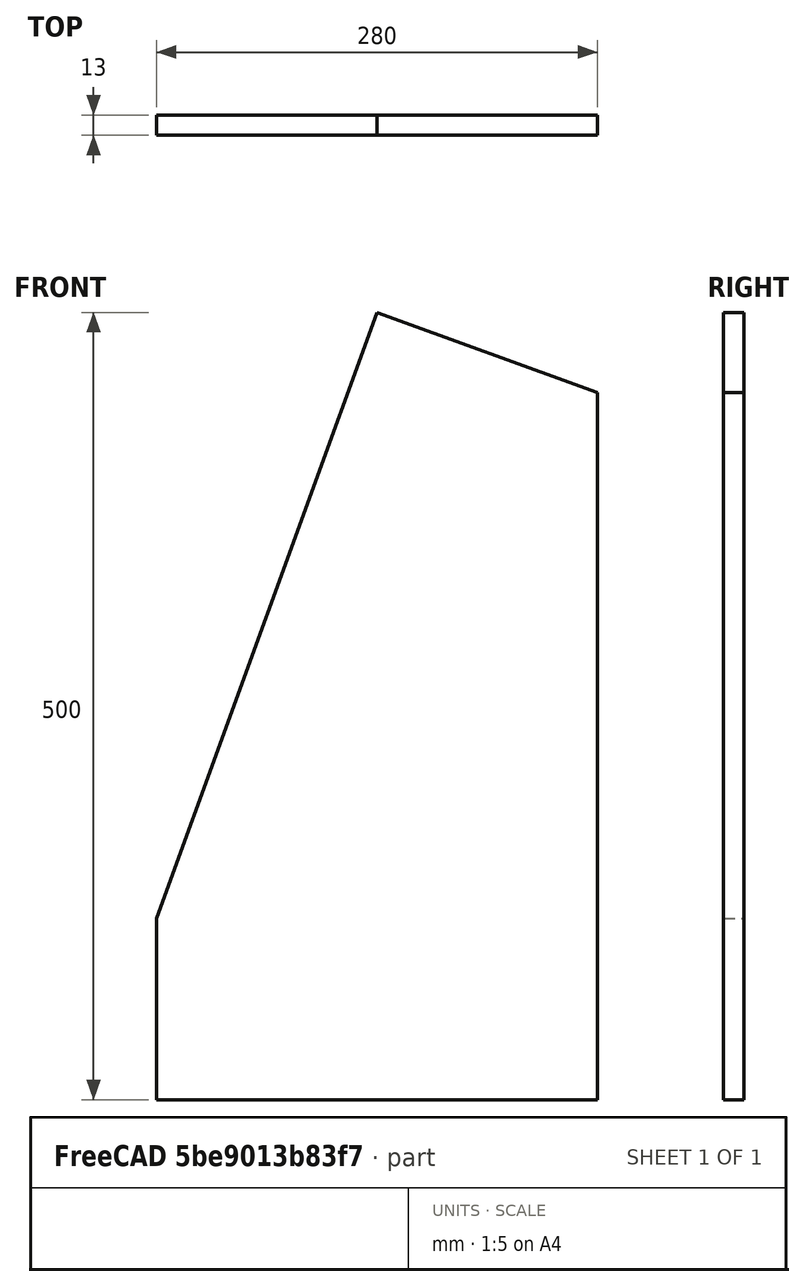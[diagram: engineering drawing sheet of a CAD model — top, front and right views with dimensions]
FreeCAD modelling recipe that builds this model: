
FCSTD DOCUMENT  (FreeCAD 0.18R14555 (Git shallow))
Label: 4000_Body_Side
License: All rights reserved
LicenseURL: http://en.wikipedia.org/wiki/All_rights_reserved
objects: Sketcher::SketchObject×1, PartDesign::Pad×1, PartDesign::Body×1, Spreadsheet::Sheet×1
note: 4 computed .brp shape members not serialized (recipe doc carries the construction recipe); baked Part::Feature solids carry a one-line shape summary decoded from their .brp

FEATURE [Sketcher::SketchObject] Sketch  label="SideWall"
  MapMode = 5
  Placement = pos=(0,0,0) rot=(1,0,0;1.5708rad)
  Support = -> [XZ_Plane]
  expr: Constraints[1] = XLS.FH
  expr: Constraints[9] = XLS.TH
  expr: Constraints[3] = XLS.TW
  sketch-geometry (7):
    g0: LineSegment StartX=0 StartY=0 StartZ=0 EndX=280 EndY=0 EndZ=0
    g1: LineSegment StartX=280 StartY=449.091 StartZ=0 EndX=140.129 EndY=500 EndZ=0
    g2: LineSegment StartX=140.129 StartY=500 StartZ=0 EndX=0 EndY=115 EndZ=0
    g3: LineSegment StartX=0 StartY=115 StartZ=0 EndX=0 EndY=0 EndZ=0
    g4: LineSegment [constr] StartX=280 StartY=449.091 StartZ=0 EndX=280 EndY=500 EndZ=0
    g5: LineSegment [constr] StartX=280 StartY=500 StartZ=0 EndX=140.129 EndY=500 EndZ=0
    g6: LineSegment StartX=280 StartY=0 StartZ=0 EndX=280 EndY=449.091 EndZ=0
  constraints (20):
    c: Coincident(g1,g2)
    c: DistanceY(g3,g3) = 115
    c: Coincident(g0,g3)
    c: DistanceX(g0,g0) = 280
    c: Coincident(g2,g3)
    c: Angle(g0,g2) = 1.22173
    c: Angle(g2,g1) = 1.5708
    c: Coincident(g5,g4)
    c: Coincident(g5,g1)
    c: DistanceY(g0,g4) = 500
    c: PointOnObject(g0,g-2)
    c: Horizontal(g0)
    c: Coincident(g6,g0)
    c: Coincident(g6,g1)
    c: Vertical(g6)
    c: Coincident(g4,g1)
    c: Vertical(g4)
    c: PointOnObject(g0,g-1)
    c: Perpendicular(g4,g5)
    c: Vertical(g3)
FEATURE [PartDesign::Pad] Pad
  Length = 13
  Length2 = 100
  Placement = pos=(0,0,0) rot=(1,0,0;1.5708rad)
  Profile = -> Sketch
  Reversed = true
  Type = 0
FEATURE [PartDesign::Body] Body
  Group = -> [Sketch,Pad]
  Origin = -> Origin
  Tip = -> Pad
FEATURE [Spreadsheet::Sheet] Spreadsheet  label="XLS"
  cells = B3=SideWall.; B4=Width; C4=TW; D4(TW)=280; E4=mm; B5=Total Height; C5=TH; D5(TH)=500; E5=mm; B6=Thickness; C6=T; D6(T)=13; E6=mm; B7=Front Height; C7=FH; D7(FH)=115; E7=mm
